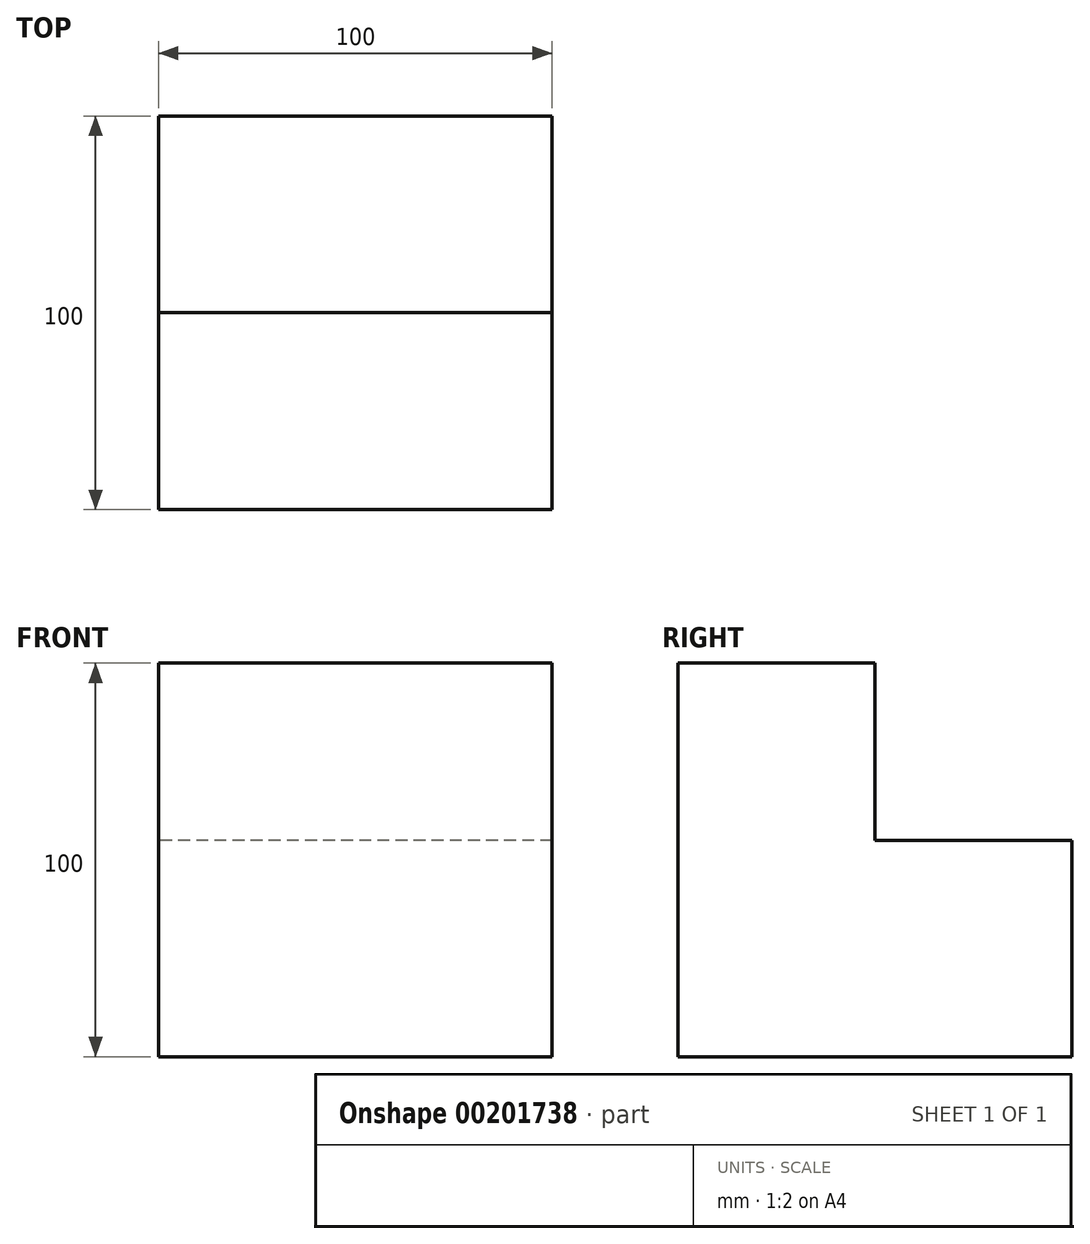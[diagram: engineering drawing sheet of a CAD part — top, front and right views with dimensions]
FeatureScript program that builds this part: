
annotation { "Feature Type Name" : "Feature", "Feature Type Description" : "" }
export const myFeature = defineFeature(function(context is Context, id is Id, definition is map)
    precondition{}
    {
        {
            var Q0;
            Q0=qCreatedBy(makeId("Right.planeOp"),FACE);
            var sketch = newSketch(context, id + "F0", { "sketchPlane" : qUnion([Q0])});
            skLineSegment(sketch, "E0", {"start": v(0, 100) * mm, "end": v(0, 0) * mm});
            skLineSegment(sketch, "E1", {"start": v(0, 0) * mm, "end": v(100, 0) * mm});
            skLineSegment(sketch, "E2", {"start": v(100, 0) * mm, "end": v(100, 55) * mm});
            skLineSegment(sketch, "E3", {"start": v(100, 55) * mm, "end": v(50, 55) * mm});
            skLineSegment(sketch, "E4", {"start": v(0, 100) * mm, "end": v(50, 100) * mm});
            skLineSegment(sketch, "E5", {"start": v(50, 100) * mm, "end": v(50, 55) * mm});
            skArc(sketch, "E6", {"start": v(63.75, 0) * mm, "mid": v(50, 13.75) * mm, "end": v(36.25, 0) * mm});
            skSolve(sketch);
        }
        {
            var Q0;
            Q0 = qSketchRegion(id + "F0", true);
            extrude(context, id + "F1", {"entities" : qUnion([Q0]), "depth" : 100 * mm});
        }
    });
